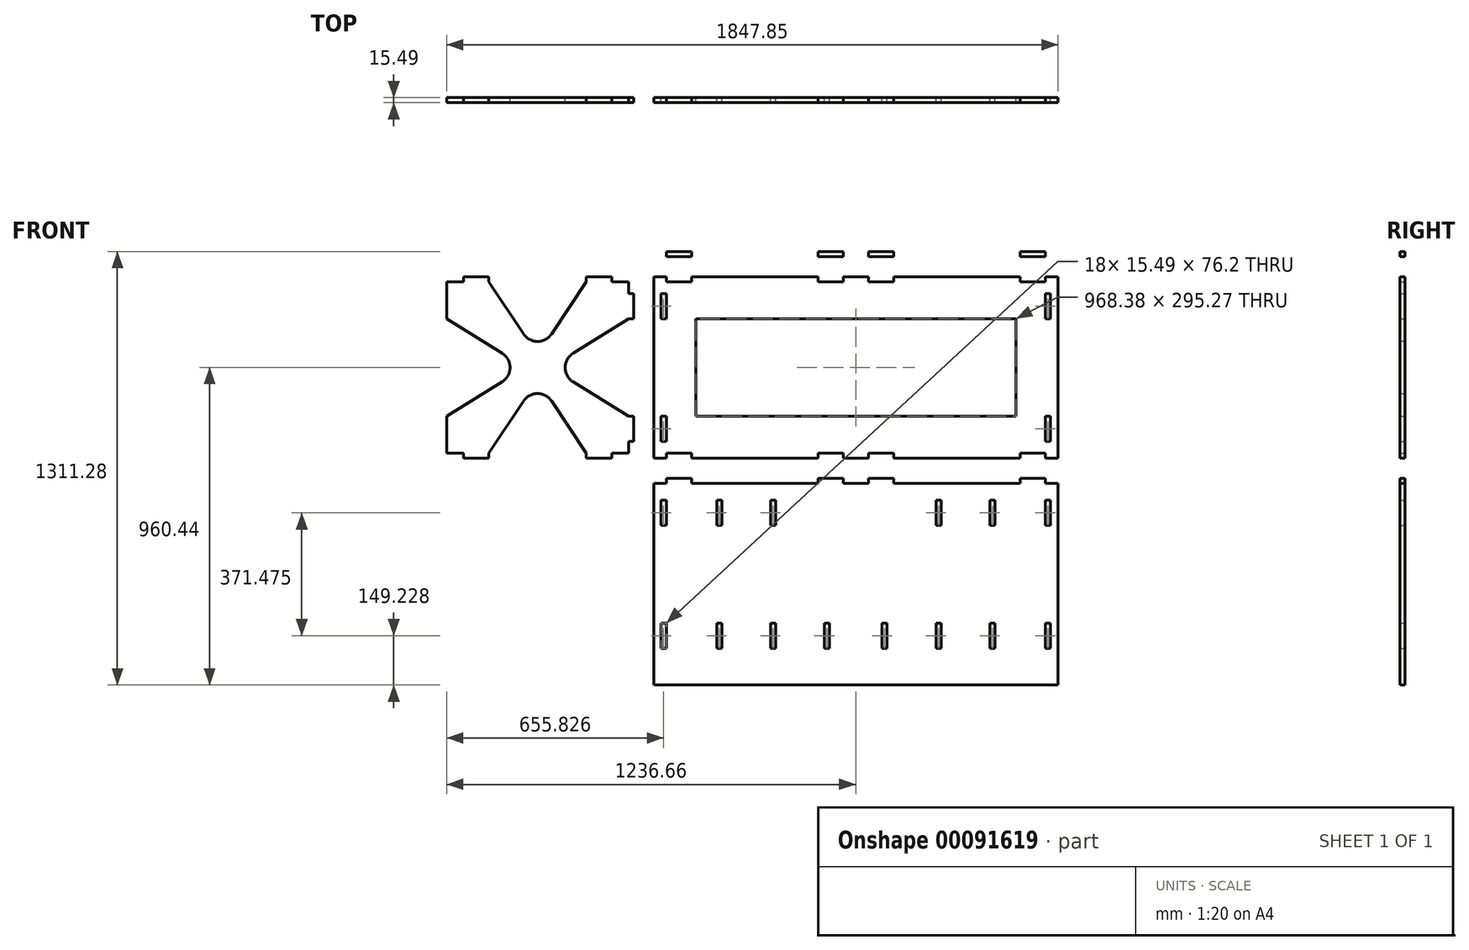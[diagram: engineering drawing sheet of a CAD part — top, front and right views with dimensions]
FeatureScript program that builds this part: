
annotation { "Feature Type Name" : "Feature", "Feature Type Description" : "" }
export const myFeature = defineFeature(function(context is Context, id is Id, definition is map)
    precondition{}
    {
        {
            var Q0;
            Q0=qCreatedBy(makeId("Front.planeOp"),FACE);
            var sketch = newSketch(context, id + "F0", { "sketchPlane" : qUnion([Q0])});
            skLineSegment(sketch, "E0.bottom", {"start": v(611.19, 274.64) * mm, "end": v(-611.19, 274.64) * mm});
            skLineSegment(sketch, "E0.top", {"start": v(611.19, -274.64) * mm, "end": v(-611.19, -274.64) * mm});
            skLineSegment(sketch, "E0.left", {"start": v(611.19, 274.64) * mm, "end": v(611.19, -274.64) * mm});
            skLineSegment(sketch, "E0.right", {"start": v(-611.19, 274.64) * mm, "end": v(-611.19, -274.64) * mm});
            skPoint(sketch, "E0.middle", {"position": v(0, 0) * mm});
            skLineSegment(sketch, "E1.bottom", {"start": v(-573.09, 274.64) * mm, "end": v(-496.89, 274.64) * mm});
            skLineSegment(sketch, "E1.top", {"start": v(-573.09, 258.89) * mm, "end": v(-496.89, 258.89) * mm});
            skLineSegment(sketch, "E1.left", {"start": v(-573.09, 274.64) * mm, "end": v(-573.09, 258.89) * mm});
            skLineSegment(sketch, "E1.right", {"start": v(-496.89, 274.64) * mm, "end": v(-496.89, 258.89) * mm});
            skLineSegment(sketch, "E2", {"start": v(0, 274.64) * mm, "end": v(0, -274.64) * mm, "construction": true});
            skLineSegment(sketch, "E3", {"start": v(-611.19, 0) * mm, "end": v(0, 0) * mm, "construction": true});
            skLineSegment(sketch, "E4", {"start": v(-305.6, -274.64) * mm, "end": v(-305.6, 274.64) * mm, "construction": true});
            skPoint(sketch, "E4.startSnap0", {"position": v(-305.6, 0) * mm});
            skLineSegment(sketch, "E5.MirrorCS", {"start": v(-114.3, 274.64) * mm, "end": v(-114.3, 258.89) * mm});
            skLineSegment(sketch, "E6.MirrorCS", {"start": v(-38.1, 274.64) * mm, "end": v(-38.1, 258.89) * mm});
            skLineSegment(sketch, "E7.MirrorCS", {"start": v(-38.1, 258.89) * mm, "end": v(-114.3, 258.89) * mm});
            skLineSegment(sketch, "E8.MirrorCS", {"start": v(-38.1, 274.64) * mm, "end": v(-114.3, 274.64) * mm});
            skLineSegment(sketch, "E9.MirrorCS", {"start": v(-38.1, -274.64) * mm, "end": v(-38.1, -258.89) * mm});
            skLineSegment(sketch, "E10.MirrorCS", {"start": v(-114.3, -274.64) * mm, "end": v(-114.3, -258.89) * mm});
            skLineSegment(sketch, "E11.MirrorCS", {"start": v(-496.89, -274.64) * mm, "end": v(-496.89, -258.89) * mm});
            skLineSegment(sketch, "E12.MirrorCS", {"start": v(-573.09, -274.64) * mm, "end": v(-573.09, -258.89) * mm});
            skLineSegment(sketch, "E13.MirrorCS", {"start": v(-38.1, -274.64) * mm, "end": v(-114.3, -274.64) * mm});
            skLineSegment(sketch, "E14.MirrorCS", {"start": v(-38.1, -258.89) * mm, "end": v(-114.3, -258.89) * mm});
            skLineSegment(sketch, "E15.MirrorCS", {"start": v(-573.09, -274.64) * mm, "end": v(-496.89, -274.64) * mm});
            skLineSegment(sketch, "E16.MirrorCS", {"start": v(-573.09, -258.89) * mm, "end": v(-496.89, -258.89) * mm});
            skLineSegment(sketch, "E17.MirrorCS", {"start": v(38.1, 274.64) * mm, "end": v(38.1, 258.89) * mm});
            skLineSegment(sketch, "E18.MirrorCS", {"start": v(114.3, 274.64) * mm, "end": v(114.3, 258.89) * mm});
            skLineSegment(sketch, "E19.MirrorCS", {"start": v(496.89, 274.64) * mm, "end": v(496.89, 258.89) * mm});
            skLineSegment(sketch, "E20.MirrorCS", {"start": v(573.09, 274.64) * mm, "end": v(573.09, 258.89) * mm});
            skLineSegment(sketch, "E21.MirrorCS", {"start": v(573.09, 274.64) * mm, "end": v(496.89, 274.64) * mm});
            skLineSegment(sketch, "E22.MirrorCS", {"start": v(573.09, 258.89) * mm, "end": v(496.89, 258.89) * mm});
            skLineSegment(sketch, "E23.MirrorCS", {"start": v(38.1, 274.64) * mm, "end": v(114.3, 274.64) * mm});
            skLineSegment(sketch, "E24.MirrorCS", {"start": v(38.1, 258.89) * mm, "end": v(114.3, 258.89) * mm});
            skLineSegment(sketch, "E25.MirrorCS", {"start": v(573.09, -274.64) * mm, "end": v(573.09, -258.89) * mm});
            skLineSegment(sketch, "E26.MirrorCS", {"start": v(496.89, -274.64) * mm, "end": v(496.89, -258.89) * mm});
            skLineSegment(sketch, "E27.MirrorCS", {"start": v(114.3, -274.64) * mm, "end": v(114.3, -258.89) * mm});
            skLineSegment(sketch, "E28.MirrorCS", {"start": v(38.1, -274.64) * mm, "end": v(38.1, -258.89) * mm});
            skLineSegment(sketch, "E29.MirrorCS", {"start": v(573.09, -258.89) * mm, "end": v(496.89, -258.89) * mm});
            skLineSegment(sketch, "E30.MirrorCS", {"start": v(573.09, -274.64) * mm, "end": v(496.89, -274.64) * mm});
            skLineSegment(sketch, "E31.MirrorCS", {"start": v(38.1, -274.64) * mm, "end": v(114.3, -274.64) * mm});
            skLineSegment(sketch, "E32.MirrorCS", {"start": v(38.1, -258.89) * mm, "end": v(114.3, -258.89) * mm});
            skLineSegment(sketch, "E33.bottom", {"start": v(-573.09, 223.84) * mm, "end": v(-588.58, 223.84) * mm});
            skLineSegment(sketch, "E33.top", {"start": v(-573.09, 147.64) * mm, "end": v(-588.58, 147.64) * mm});
            skLineSegment(sketch, "E33.left", {"start": v(-573.09, 223.84) * mm, "end": v(-573.09, 147.64) * mm});
            skLineSegment(sketch, "E33.right", {"start": v(-588.58, 223.84) * mm, "end": v(-588.58, 147.64) * mm});
            skLineSegment(sketch, "E34.MirrorCS", {"start": v(-573.09, -223.84) * mm, "end": v(-573.09, -147.64) * mm});
            skLineSegment(sketch, "E35.MirrorCS", {"start": v(-588.58, -223.84) * mm, "end": v(-588.58, -147.64) * mm});
            skLineSegment(sketch, "E36.MirrorCS", {"start": v(-573.09, -147.64) * mm, "end": v(-588.58, -147.64) * mm});
            skLineSegment(sketch, "E37.MirrorCS", {"start": v(-573.09, -223.84) * mm, "end": v(-588.58, -223.84) * mm});
            skLineSegment(sketch, "E38.MirrorCS", {"start": v(573.09, -223.84) * mm, "end": v(588.58, -223.84) * mm});
            skLineSegment(sketch, "E39.MirrorCS", {"start": v(573.09, -147.64) * mm, "end": v(588.58, -147.64) * mm});
            skLineSegment(sketch, "E40.MirrorCS", {"start": v(573.09, 223.84) * mm, "end": v(588.58, 223.84) * mm});
            skLineSegment(sketch, "E41.MirrorCS", {"start": v(573.09, 147.64) * mm, "end": v(588.58, 147.64) * mm});
            skLineSegment(sketch, "E42.MirrorCS", {"start": v(573.09, 223.84) * mm, "end": v(573.09, 147.64) * mm});
            skLineSegment(sketch, "E43.MirrorCS", {"start": v(588.58, 223.84) * mm, "end": v(588.58, 147.64) * mm});
            skLineSegment(sketch, "E44.MirrorCS", {"start": v(588.58, -223.84) * mm, "end": v(588.58, -147.64) * mm});
            skLineSegment(sketch, "E45.MirrorCS", {"start": v(573.09, -223.84) * mm, "end": v(573.09, -147.64) * mm});
            skLineSegment(sketch, "E46.bottom", {"start": v(-611.19, 350.84) * mm, "end": v(-3.17, 350.84) * mm});
            skLineSegment(sketch, "E46.top", {"start": v(-611.19, 960.44) * mm, "end": v(-3.18, 960.44) * mm});
            skLineSegment(sketch, "E46.left", {"start": v(-611.19, 350.84) * mm, "end": v(-611.19, 960.44) * mm});
            skLineSegment(sketch, "E46.right", {"start": v(-3.17, 350.84) * mm, "end": v(-3.18, 960.44) * mm});
            skLineSegment(sketch, "E47.bottom", {"start": v(611.19, 350.84) * mm, "end": v(0, 350.84) * mm});
            skLineSegment(sketch, "E47.top", {"start": v(611.19, 960.44) * mm, "end": v(0, 960.44) * mm});
            skLineSegment(sketch, "E47.left", {"start": v(611.19, 350.84) * mm, "end": v(611.19, 960.44) * mm});
            skLineSegment(sketch, "E47.right", {"start": v(0, 350.84) * mm, "end": v(0, 960.44) * mm});
            skLineSegment(sketch, "E48", {"start": v(-76.2, 258.89) * mm, "end": v(-76.2, 350.84) * mm, "construction": true});
            skLineSegment(sketch, "E49", {"start": v(-76.2, 304.86) * mm, "end": v(-114.3, 304.86) * mm, "construction": true});
            skPoint(sketch, "E49.endSnap0", {"position": v(-76.2, 304.86) * mm});
            skLineSegment(sketch, "E50.MirrorCS", {"start": v(496.89, 335.09) * mm, "end": v(496.89, 350.84) * mm});
            skLineSegment(sketch, "E51.MirrorCS", {"start": v(573.09, 335.09) * mm, "end": v(573.09, 350.84) * mm});
            skLineSegment(sketch, "E52.MirrorCS", {"start": v(114.3, 335.09) * mm, "end": v(114.3, 350.84) * mm});
            skLineSegment(sketch, "E53.MirrorCS", {"start": v(-573.09, 335.09) * mm, "end": v(-573.09, 350.84) * mm});
            skLineSegment(sketch, "E54.MirrorCS", {"start": v(-496.89, 335.09) * mm, "end": v(-496.89, 350.84) * mm});
            skLineSegment(sketch, "E55.MirrorCS", {"start": v(38.1, 335.09) * mm, "end": v(38.1, 350.84) * mm});
            skLineSegment(sketch, "E56.MirrorCS", {"start": v(-38.1, 335.09) * mm, "end": v(-38.1, 350.84) * mm});
            skLineSegment(sketch, "E57.MirrorCS", {"start": v(-114.3, 335.09) * mm, "end": v(-114.3, 350.84) * mm});
            skLineSegment(sketch, "E58.MirrorCS", {"start": v(-38.1, 335.09) * mm, "end": v(-114.3, 335.09) * mm});
            skLineSegment(sketch, "E59.MirrorCS", {"start": v(-38.1, 350.84) * mm, "end": v(-114.3, 350.84) * mm});
            skLineSegment(sketch, "E60.MirrorCS", {"start": v(-573.09, 335.09) * mm, "end": v(-496.89, 335.09) * mm});
            skLineSegment(sketch, "E61.MirrorCS", {"start": v(-573.09, 350.84) * mm, "end": v(-496.89, 350.84) * mm});
            skLineSegment(sketch, "E62.MirrorCS", {"start": v(573.09, 335.09) * mm, "end": v(496.89, 335.09) * mm});
            skLineSegment(sketch, "E63.MirrorCS", {"start": v(38.1, 335.09) * mm, "end": v(114.3, 335.09) * mm});
            skLineSegment(sketch, "E64.MirrorCS", {"start": v(573.09, 350.84) * mm, "end": v(496.89, 350.84) * mm});
            skLineSegment(sketch, "E65.MirrorCS", {"start": v(38.1, 350.84) * mm, "end": v(114.3, 350.84) * mm});
            skLineSegment(sketch, "E66", {"start": v(-611.19, 350.84) * mm, "end": v(-611.19, 274.64) * mm, "construction": true});
            skLineSegment(sketch, "E67", {"start": v(-611.19, 312.74) * mm, "end": v(-496.89, 312.74) * mm, "construction": true});
            skLineSegment(sketch, "E68.MirrorCS", {"start": v(-573.09, 773.11) * mm, "end": v(-588.58, 773.11) * mm});
            skLineSegment(sketch, "E69.MirrorCS", {"start": v(-573.09, 477.84) * mm, "end": v(-588.58, 477.84) * mm});
            skLineSegment(sketch, "E70.MirrorCS", {"start": v(-573.09, 401.64) * mm, "end": v(-588.58, 401.64) * mm});
            skLineSegment(sketch, "E71.MirrorCS", {"start": v(-573.09, 849.31) * mm, "end": v(-588.58, 849.31) * mm});
            skLineSegment(sketch, "E72.MirrorCS", {"start": v(-588.58, 401.64) * mm, "end": v(-588.58, 477.84) * mm});
            skLineSegment(sketch, "E73.MirrorCS", {"start": v(-573.09, 849.31) * mm, "end": v(-573.09, 773.11) * mm});
            skLineSegment(sketch, "E74.MirrorCS", {"start": v(-573.09, 401.64) * mm, "end": v(-573.09, 477.84) * mm});
            skLineSegment(sketch, "E75.MirrorCS", {"start": v(-588.58, 849.31) * mm, "end": v(-588.58, 773.11) * mm});
            skLineSegment(sketch, "E76.MirrorCS", {"start": v(573.09, 477.84) * mm, "end": v(588.58, 477.84) * mm});
            skLineSegment(sketch, "E77.MirrorCS", {"start": v(573.09, 401.64) * mm, "end": v(588.58, 401.64) * mm});
            skLineSegment(sketch, "E78.MirrorCS", {"start": v(573.09, 773.11) * mm, "end": v(588.58, 773.11) * mm});
            skLineSegment(sketch, "E79.MirrorCS", {"start": v(573.09, 849.31) * mm, "end": v(588.58, 849.31) * mm});
            skLineSegment(sketch, "E80.MirrorCS", {"start": v(573.09, 401.64) * mm, "end": v(573.09, 477.84) * mm});
            skLineSegment(sketch, "E81.MirrorCS", {"start": v(588.58, 849.31) * mm, "end": v(588.58, 773.11) * mm});
            skLineSegment(sketch, "E82.MirrorCS", {"start": v(573.09, 849.31) * mm, "end": v(573.09, 773.11) * mm});
            skLineSegment(sketch, "E83.MirrorCS", {"start": v(588.58, 401.64) * mm, "end": v(588.58, 477.84) * mm});
            skLineSegment(sketch, "E84.bottom", {"start": v(-687.39, 258.89) * mm, "end": v(-1236.66, 258.89) * mm});
            skLineSegment(sketch, "E84.top", {"start": v(-687.39, -258.89) * mm, "end": v(-1236.66, -258.89) * mm});
            skLineSegment(sketch, "E84.left", {"start": v(-687.39, 258.89) * mm, "end": v(-687.39, -258.89) * mm});
            skLineSegment(sketch, "E84.right", {"start": v(-1236.66, 258.89) * mm, "end": v(-1236.66, -258.89) * mm});
            skLineSegment(sketch, "E85", {"start": v(-738.19, 258.89) * mm, "end": v(-738.19, 274.38) * mm});
            skLineSegment(sketch, "E86", {"start": v(-738.19, 274.38) * mm, "end": v(-814.39, 274.38) * mm});
            skLineSegment(sketch, "E87", {"start": v(-814.39, 274.38) * mm, "end": v(-814.39, 258.89) * mm});
            skLineSegment(sketch, "E88", {"start": v(-687.39, 223.84) * mm, "end": v(-671.9, 223.84) * mm});
            skLineSegment(sketch, "E89", {"start": v(-671.9, 223.84) * mm, "end": v(-671.9, 147.64) * mm});
            skLineSegment(sketch, "E90", {"start": v(-671.9, 147.64) * mm, "end": v(-687.39, 147.64) * mm});
            skLineSegment(sketch, "E91.MirrorCS", {"start": v(-687.39, -223.84) * mm, "end": v(-671.9, -223.84) * mm});
            skLineSegment(sketch, "E92.MirrorCS", {"start": v(-671.9, -147.64) * mm, "end": v(-687.39, -147.64) * mm});
            skLineSegment(sketch, "E93.MirrorCS", {"start": v(-671.9, -223.84) * mm, "end": v(-671.9, -147.64) * mm});
            skLineSegment(sketch, "E94", {"start": v(-962.03, 258.89) * mm, "end": v(-962.03, -258.89) * mm, "construction": true});
            skLineSegment(sketch, "E95", {"start": v(-962.03, -38.1) * mm, "end": v(-1109.66, -258.89) * mm});
            skLineSegment(sketch, "E96", {"start": v(-962.03, -38.1) * mm, "end": v(-814.39, -258.89) * mm});
            skLineSegment(sketch, "E97.bottom", {"start": v(-1000.13, 38.1) * mm, "end": v(-923.93, 38.1) * mm, "construction": true});
            skLineSegment(sketch, "E97.top", {"start": v(-1000.13, -38.1) * mm, "end": v(-923.93, -38.1) * mm, "construction": true});
            skLineSegment(sketch, "E97.left", {"start": v(-1000.13, 38.1) * mm, "end": v(-1000.13, -38.1) * mm, "construction": true});
            skLineSegment(sketch, "E97.right", {"start": v(-923.93, 38.1) * mm, "end": v(-923.93, -38.1) * mm, "construction": true});
            skPoint(sketch, "E97.middle", {"position": v(-962.03, 0) * mm});
            skLineSegment(sketch, "E98", {"start": v(-1000.13, 0) * mm, "end": v(-1236.66, 147.64) * mm});
            skLineSegment(sketch, "E99", {"start": v(-1000.13, 0) * mm, "end": v(-1236.66, -147.64) * mm});
            skLineSegment(sketch, "E100", {"start": v(-962.03, 38.1) * mm, "end": v(-1109.66, 258.89) * mm});
            skLineSegment(sketch, "E101", {"start": v(-814.39, 258.89) * mm, "end": v(-962.03, 38.1) * mm});
            skLineSegment(sketch, "E102", {"start": v(-923.93, 0) * mm, "end": v(-687.39, 147.64) * mm});
            skLineSegment(sketch, "E103", {"start": v(-923.93, 0) * mm, "end": v(-687.39, -147.64) * mm});
            skLineSegment(sketch, "E104.MirrorCS", {"start": v(-573.09, -849.31) * mm, "end": v(-588.58, -849.31) * mm});
            skLineSegment(sketch, "E105.MirrorCS", {"start": v(-573.09, -773.11) * mm, "end": v(-588.58, -773.11) * mm});
            skLineSegment(sketch, "E106.MirrorCS", {"start": v(-573.09, -401.64) * mm, "end": v(-588.58, -401.64) * mm});
            skLineSegment(sketch, "E107.MirrorCS", {"start": v(-114.3, -335.09) * mm, "end": v(-114.3, -350.84) * mm});
            skLineSegment(sketch, "E108.MirrorCS", {"start": v(114.3, -335.09) * mm, "end": v(114.3, -350.84) * mm});
            skLineSegment(sketch, "E109.MirrorCS", {"start": v(-573.09, -477.84) * mm, "end": v(-588.58, -477.84) * mm});
            skLineSegment(sketch, "E110.MirrorCS", {"start": v(-573.09, -335.09) * mm, "end": v(-573.09, -350.84) * mm});
            skLineSegment(sketch, "E111.MirrorCS", {"start": v(-496.89, -335.09) * mm, "end": v(-496.89, -350.84) * mm});
            skLineSegment(sketch, "E112.MirrorCS", {"start": v(38.1, -335.09) * mm, "end": v(38.1, -350.84) * mm});
            skLineSegment(sketch, "E113.MirrorCS", {"start": v(-38.1, -335.09) * mm, "end": v(-38.1, -350.84) * mm});
            skLineSegment(sketch, "E114.MirrorCS", {"start": v(573.09, -477.84) * mm, "end": v(588.58, -477.84) * mm});
            skLineSegment(sketch, "E115.MirrorCS", {"start": v(573.09, -773.11) * mm, "end": v(588.58, -773.11) * mm});
            skLineSegment(sketch, "E116.MirrorCS", {"start": v(573.09, -401.64) * mm, "end": v(588.58, -401.64) * mm});
            skLineSegment(sketch, "E117.MirrorCS", {"start": v(573.09, -849.31) * mm, "end": v(588.58, -849.31) * mm});
            skLineSegment(sketch, "E118.MirrorCS", {"start": v(496.89, -335.09) * mm, "end": v(496.89, -350.84) * mm});
            skLineSegment(sketch, "E119.MirrorCS", {"start": v(573.09, -335.09) * mm, "end": v(573.09, -350.84) * mm});
            skLineSegment(sketch, "E120.MirrorCS", {"start": v(-38.1, -335.09) * mm, "end": v(-114.3, -335.09) * mm});
            skLineSegment(sketch, "E121.MirrorCS", {"start": v(-38.1, -350.84) * mm, "end": v(-114.3, -350.84) * mm});
            skLineSegment(sketch, "E122.MirrorCS", {"start": v(-588.58, -401.64) * mm, "end": v(-588.58, -477.84) * mm});
            skLineSegment(sketch, "E123.MirrorCS", {"start": v(-573.09, -849.31) * mm, "end": v(-573.09, -773.11) * mm});
            skLineSegment(sketch, "E124.MirrorCS", {"start": v(-573.09, -401.64) * mm, "end": v(-573.09, -477.84) * mm});
            skLineSegment(sketch, "E125.MirrorCS", {"start": v(-588.58, -849.31) * mm, "end": v(-588.58, -773.11) * mm});
            skLineSegment(sketch, "E126.MirrorCS", {"start": v(-573.09, -335.09) * mm, "end": v(-496.89, -335.09) * mm});
            skLineSegment(sketch, "E127.MirrorCS", {"start": v(573.09, -335.09) * mm, "end": v(496.89, -335.09) * mm});
            skLineSegment(sketch, "E128.MirrorCS", {"start": v(-573.09, -350.84) * mm, "end": v(-496.89, -350.84) * mm});
            skLineSegment(sketch, "E129.MirrorCS", {"start": v(38.1, -335.09) * mm, "end": v(114.3, -335.09) * mm});
            skLineSegment(sketch, "E130.MirrorCS", {"start": v(573.09, -350.84) * mm, "end": v(496.89, -350.84) * mm});
            skLineSegment(sketch, "E131.MirrorCS", {"start": v(573.09, -401.64) * mm, "end": v(573.09, -477.84) * mm});
            skLineSegment(sketch, "E132.MirrorCS", {"start": v(588.58, -849.31) * mm, "end": v(588.58, -773.11) * mm});
            skLineSegment(sketch, "E133.MirrorCS", {"start": v(38.1, -350.84) * mm, "end": v(114.3, -350.84) * mm});
            skLineSegment(sketch, "E134.MirrorCS", {"start": v(573.09, -849.31) * mm, "end": v(573.09, -773.11) * mm});
            skLineSegment(sketch, "E135.MirrorCS", {"start": v(588.58, -401.64) * mm, "end": v(588.58, -477.84) * mm});
            skLineSegment(sketch, "E136.MirrorCS", {"start": v(-611.19, -350.84) * mm, "end": v(-611.19, -960.44) * mm});
            skLineSegment(sketch, "E137.MirrorCS", {"start": v(611.19, -350.84) * mm, "end": v(611.19, -960.44) * mm});
            skLineSegment(sketch, "E138", {"start": v(-611.19, -350.84) * mm, "end": v(611.19, -350.84) * mm});
            skLineSegment(sketch, "E139", {"start": v(611.19, -960.44) * mm, "end": v(-611.19, -960.44) * mm});
            skLineSegment(sketch, "E140.MirrorCS", {"start": v(-738.19, -258.89) * mm, "end": v(-738.19, -274.38) * mm});
            skLineSegment(sketch, "E141.MirrorCS", {"start": v(-814.39, -274.38) * mm, "end": v(-814.39, -258.89) * mm});
            skLineSegment(sketch, "E142.MirrorCS", {"start": v(-738.19, -274.38) * mm, "end": v(-814.39, -274.38) * mm});
            skLineSegment(sketch, "E143", {"start": v(-496.89, 223.84) * mm, "end": v(-496.89, -223.84) * mm, "construction": true});
            skLineSegment(sketch, "E144", {"start": v(-738.19, -350.84) * mm, "end": v(-1185.86, -350.84) * mm});
            skPoint(sketch, "E145", {"position": v(-962.03, -350.84) * mm});
            skLineSegment(sketch, "E146.MirrorCS", {"start": v(-1109.66, -274.38) * mm, "end": v(-1109.66, -258.89) * mm});
            skLineSegment(sketch, "E147.MirrorCS", {"start": v(-1185.86, -274.38) * mm, "end": v(-1109.66, -274.38) * mm});
            skLineSegment(sketch, "E148.MirrorCS", {"start": v(-1185.86, -258.89) * mm, "end": v(-1185.86, -274.38) * mm});
            skLineSegment(sketch, "E149.MirrorCS", {"start": v(-1185.86, 258.89) * mm, "end": v(-1185.86, 274.38) * mm});
            skLineSegment(sketch, "E150.MirrorCS", {"start": v(-1185.86, 274.38) * mm, "end": v(-1109.66, 274.38) * mm});
            skLineSegment(sketch, "E151.MirrorCS", {"start": v(-1109.66, 274.38) * mm, "end": v(-1109.66, 258.89) * mm});
            skLineSegment(sketch, "E152", {"start": v(-333.98, 960.44) * mm, "end": v(-333.98, 350.84) * mm, "construction": true});
            skLineSegment(sketch, "E153.MirrorCS", {"start": v(-94.87, 477.84) * mm, "end": v(-79.37, 477.84) * mm});
            skLineSegment(sketch, "E154.MirrorCS", {"start": v(-94.87, 773.11) * mm, "end": v(-79.38, 773.11) * mm});
            skLineSegment(sketch, "E155.MirrorCS", {"start": v(-94.87, 401.64) * mm, "end": v(-79.38, 401.64) * mm});
            skLineSegment(sketch, "E156.MirrorCS", {"start": v(-94.87, 849.31) * mm, "end": v(-79.38, 849.31) * mm});
            skLineSegment(sketch, "E157.MirrorCS", {"start": v(-79.37, 401.64) * mm, "end": v(-79.37, 477.84) * mm});
            skLineSegment(sketch, "E158.MirrorCS", {"start": v(-94.87, 849.31) * mm, "end": v(-94.87, 773.11) * mm});
            skLineSegment(sketch, "E159.MirrorCS", {"start": v(-79.38, 849.31) * mm, "end": v(-79.38, 773.11) * mm});
            skLineSegment(sketch, "E160.MirrorCS", {"start": v(-94.87, 401.64) * mm, "end": v(-94.87, 477.84) * mm});
            skLineSegment(sketch, "E161.MirrorCS", {"start": v(94.87, 477.84) * mm, "end": v(79.37, 477.84) * mm});
            skLineSegment(sketch, "E162.MirrorCS", {"start": v(94.87, 773.11) * mm, "end": v(79.37, 773.11) * mm});
            skLineSegment(sketch, "E163.MirrorCS", {"start": v(94.87, 401.64) * mm, "end": v(79.37, 401.64) * mm});
            skLineSegment(sketch, "E164.MirrorCS", {"start": v(94.87, 849.31) * mm, "end": v(79.37, 849.31) * mm});
            skLineSegment(sketch, "E165.MirrorCS", {"start": v(79.37, 849.31) * mm, "end": v(79.37, 773.11) * mm});
            skLineSegment(sketch, "E166.MirrorCS", {"start": v(94.87, 401.64) * mm, "end": v(94.87, 477.84) * mm});
            skLineSegment(sketch, "E167.MirrorCS", {"start": v(94.87, 849.31) * mm, "end": v(94.87, 773.11) * mm});
            skLineSegment(sketch, "E168.MirrorCS", {"start": v(79.37, 401.64) * mm, "end": v(79.37, 477.84) * mm});
            skLineSegment(sketch, "E169.bottom", {"start": v(-420.69, 849.31) * mm, "end": v(-405.2, 849.31) * mm});
            skLineSegment(sketch, "E169.top", {"start": v(-420.69, 773.11) * mm, "end": v(-405.2, 773.11) * mm});
            skLineSegment(sketch, "E169.left", {"start": v(-420.69, 849.31) * mm, "end": v(-420.69, 773.11) * mm});
            skLineSegment(sketch, "E169.right", {"start": v(-405.2, 849.31) * mm, "end": v(-405.2, 773.11) * mm});
            skLineSegment(sketch, "E170", {"start": v(-405.2, 811.21) * mm, "end": v(-94.87, 811.21) * mm, "construction": true});
            skLineSegment(sketch, "E171.bottom", {"start": v(-257.78, 849.31) * mm, "end": v(-242.28, 849.31) * mm});
            skLineSegment(sketch, "E171.top", {"start": v(-257.78, 773.11) * mm, "end": v(-242.28, 773.11) * mm});
            skLineSegment(sketch, "E171.left", {"start": v(-257.78, 849.31) * mm, "end": v(-257.78, 773.11) * mm});
            skLineSegment(sketch, "E171.right", {"start": v(-242.28, 849.31) * mm, "end": v(-242.28, 773.11) * mm});
            skPoint(sketch, "E171.middle", {"position": v(-250.03, 811.21) * mm});
            skLineSegment(sketch, "E172.MirrorCS", {"start": v(257.78, 773.11) * mm, "end": v(242.28, 773.11) * mm});
            skLineSegment(sketch, "E173.MirrorCS", {"start": v(420.69, 773.11) * mm, "end": v(405.2, 773.11) * mm});
            skLineSegment(sketch, "E174.MirrorCS", {"start": v(257.78, 849.31) * mm, "end": v(242.28, 849.31) * mm});
            skLineSegment(sketch, "E175.MirrorCS", {"start": v(420.69, 849.31) * mm, "end": v(405.2, 849.31) * mm});
            skLineSegment(sketch, "E176.MirrorCS", {"start": v(420.69, 849.31) * mm, "end": v(420.69, 773.11) * mm});
            skLineSegment(sketch, "E177.MirrorCS", {"start": v(405.2, 849.31) * mm, "end": v(405.2, 773.11) * mm});
            skLineSegment(sketch, "E178.MirrorCS", {"start": v(257.78, 849.31) * mm, "end": v(257.78, 773.11) * mm});
            skLineSegment(sketch, "E179.MirrorCS", {"start": v(242.28, 849.31) * mm, "end": v(242.28, 773.11) * mm});
            skPoint(sketch, "E180.MirrorP", {"position": v(250.03, 811.21) * mm});
            skLineSegment(sketch, "E181.MirrorCS", {"start": v(-420.69, -773.11) * mm, "end": v(-405.2, -773.11) * mm});
            skLineSegment(sketch, "E182.MirrorCS", {"start": v(-257.78, -773.11) * mm, "end": v(-242.28, -773.11) * mm});
            skLineSegment(sketch, "E183.MirrorCS", {"start": v(-79.37, -849.31) * mm, "end": v(-79.37, -773.11) * mm});
            skLineSegment(sketch, "E184.MirrorCS", {"start": v(94.87, -773.11) * mm, "end": v(79.38, -773.11) * mm});
            skLineSegment(sketch, "E185.MirrorCS", {"start": v(420.69, -773.11) * mm, "end": v(405.2, -773.11) * mm});
            skLineSegment(sketch, "E186.MirrorCS", {"start": v(79.38, -849.31) * mm, "end": v(79.37, -773.11) * mm});
            skLineSegment(sketch, "E187.MirrorCS", {"start": v(420.69, -849.31) * mm, "end": v(420.69, -773.11) * mm});
            skLineSegment(sketch, "E188.MirrorCS", {"start": v(94.87, -849.31) * mm, "end": v(79.38, -849.31) * mm});
            skLineSegment(sketch, "E189.MirrorCS", {"start": v(-242.28, -849.31) * mm, "end": v(-242.28, -773.11) * mm});
            skLineSegment(sketch, "E190.MirrorCS", {"start": v(-257.78, -849.31) * mm, "end": v(-242.28, -849.31) * mm});
            skLineSegment(sketch, "E191.MirrorCS", {"start": v(257.78, -849.31) * mm, "end": v(242.28, -849.31) * mm});
            skLineSegment(sketch, "E192.MirrorCS", {"start": v(-94.87, -849.31) * mm, "end": v(-79.37, -849.31) * mm});
            skLineSegment(sketch, "E193.MirrorCS", {"start": v(257.78, -849.31) * mm, "end": v(257.78, -773.11) * mm});
            skLineSegment(sketch, "E194.MirrorCS", {"start": v(242.28, -849.31) * mm, "end": v(242.28, -773.11) * mm});
            skLineSegment(sketch, "E195.MirrorCS", {"start": v(-420.69, -849.31) * mm, "end": v(-405.2, -849.31) * mm});
            skLineSegment(sketch, "E196.MirrorCS", {"start": v(-94.87, -773.11) * mm, "end": v(-79.37, -773.11) * mm});
            skLineSegment(sketch, "E197.MirrorCS", {"start": v(257.78, -773.11) * mm, "end": v(242.28, -773.11) * mm});
            skLineSegment(sketch, "E198.MirrorCS", {"start": v(-405.2, -849.31) * mm, "end": v(-405.2, -773.11) * mm});
            skLineSegment(sketch, "E199.MirrorCS", {"start": v(-420.69, -849.31) * mm, "end": v(-420.69, -773.11) * mm});
            skLineSegment(sketch, "E200.MirrorCS", {"start": v(-94.87, -849.31) * mm, "end": v(-94.87, -773.11) * mm});
            skLineSegment(sketch, "E201.MirrorCS", {"start": v(-257.78, -849.31) * mm, "end": v(-257.78, -773.11) * mm});
            skLineSegment(sketch, "E202.MirrorCS", {"start": v(420.69, -849.31) * mm, "end": v(405.2, -849.31) * mm});
            skLineSegment(sketch, "E203.MirrorCS", {"start": v(405.2, -849.31) * mm, "end": v(405.2, -773.11) * mm});
            skLineSegment(sketch, "E204.MirrorCS", {"start": v(94.87, -849.31) * mm, "end": v(94.87, -773.11) * mm});
            skPoint(sketch, "E205.MirrorP", {"position": v(250.03, -811.21) * mm});
            skPoint(sketch, "E206.MirrorP", {"position": v(-250.03, -811.21) * mm});
            skLineSegment(sketch, "E207.MirrorCS", {"start": v(-405.2, -811.21) * mm, "end": v(-94.87, -811.21) * mm, "construction": true});
            skLineSegment(sketch, "E208", {"start": v(-333.98, 849.31) * mm, "end": v(-333.98, 401.64) * mm, "construction": true});
            skLineSegment(sketch, "E209", {"start": v(-333.98, 625.48) * mm, "end": v(-420.69, 625.48) * mm, "construction": true});
            skLineSegment(sketch, "E210.MirrorCS", {"start": v(-257.78, 401.64) * mm, "end": v(-242.28, 401.64) * mm});
            skLineSegment(sketch, "E211.MirrorCS", {"start": v(-257.78, 477.84) * mm, "end": v(-242.28, 477.84) * mm});
            skLineSegment(sketch, "E212.MirrorCS", {"start": v(-420.69, 477.84) * mm, "end": v(-405.2, 477.84) * mm});
            skLineSegment(sketch, "E213.MirrorCS", {"start": v(-420.69, 401.64) * mm, "end": v(-405.2, 401.64) * mm});
            skLineSegment(sketch, "E214.MirrorCS", {"start": v(-242.28, 401.64) * mm, "end": v(-242.28, 477.84) * mm});
            skLineSegment(sketch, "E215.MirrorCS", {"start": v(-257.78, 401.64) * mm, "end": v(-257.78, 477.84) * mm});
            skLineSegment(sketch, "E216.MirrorCS", {"start": v(-405.2, 401.64) * mm, "end": v(-405.2, 477.84) * mm});
            skPoint(sketch, "E217.MirrorP", {"position": v(-250.03, 439.74) * mm});
            skLineSegment(sketch, "E218.MirrorCS", {"start": v(-420.69, 401.64) * mm, "end": v(-420.69, 477.84) * mm});
            skLineSegment(sketch, "E219.MirrorCS", {"start": v(420.69, 401.64) * mm, "end": v(405.2, 401.64) * mm});
            skLineSegment(sketch, "E220.MirrorCS", {"start": v(257.78, 401.64) * mm, "end": v(242.28, 401.64) * mm});
            skLineSegment(sketch, "E221.MirrorCS", {"start": v(257.78, 477.84) * mm, "end": v(242.28, 477.84) * mm});
            skLineSegment(sketch, "E222.MirrorCS", {"start": v(420.69, 477.84) * mm, "end": v(405.2, 477.84) * mm});
            skLineSegment(sketch, "E223.MirrorCS", {"start": v(257.78, 401.64) * mm, "end": v(257.78, 477.84) * mm});
            skLineSegment(sketch, "E224.MirrorCS", {"start": v(242.28, 401.64) * mm, "end": v(242.28, 477.84) * mm});
            skPoint(sketch, "E225.MirrorP", {"position": v(250.03, 439.74) * mm});
            skLineSegment(sketch, "E226.MirrorCS", {"start": v(420.69, 401.64) * mm, "end": v(420.69, 477.84) * mm});
            skLineSegment(sketch, "E227.MirrorCS", {"start": v(405.2, 401.64) * mm, "end": v(405.2, 477.84) * mm});
            skLineSegment(sketch, "E228.MirrorCS", {"start": v(-257.78, -477.84) * mm, "end": v(-242.28, -477.84) * mm});
            skLineSegment(sketch, "E229.MirrorCS", {"start": v(-420.69, -477.84) * mm, "end": v(-405.2, -477.84) * mm});
            skLineSegment(sketch, "E230.MirrorCS", {"start": v(-257.78, -401.64) * mm, "end": v(-242.28, -401.64) * mm});
            skLineSegment(sketch, "E231.MirrorCS", {"start": v(-420.69, -401.64) * mm, "end": v(-405.2, -401.64) * mm});
            skLineSegment(sketch, "E232.MirrorCS", {"start": v(-242.28, -401.64) * mm, "end": v(-242.28, -477.84) * mm});
            skPoint(sketch, "E233.MirrorP", {"position": v(-250.03, -439.74) * mm});
            skLineSegment(sketch, "E234.MirrorCS", {"start": v(-420.69, -401.64) * mm, "end": v(-420.69, -477.84) * mm});
            skLineSegment(sketch, "E235.MirrorCS", {"start": v(-257.78, -401.64) * mm, "end": v(-257.78, -477.84) * mm});
            skLineSegment(sketch, "E236.MirrorCS", {"start": v(-405.2, -401.64) * mm, "end": v(-405.2, -477.84) * mm});
            skLineSegment(sketch, "E237.MirrorCS", {"start": v(420.69, -401.64) * mm, "end": v(405.2, -401.64) * mm});
            skLineSegment(sketch, "E238.MirrorCS", {"start": v(257.78, -401.64) * mm, "end": v(242.28, -401.64) * mm});
            skLineSegment(sketch, "E239.MirrorCS", {"start": v(257.78, -477.84) * mm, "end": v(242.28, -477.84) * mm});
            skLineSegment(sketch, "E240.MirrorCS", {"start": v(420.69, -477.84) * mm, "end": v(405.2, -477.84) * mm});
            skLineSegment(sketch, "E241.MirrorCS", {"start": v(257.78, -401.64) * mm, "end": v(257.78, -477.84) * mm});
            skLineSegment(sketch, "E242.MirrorCS", {"start": v(242.28, -401.64) * mm, "end": v(242.28, -477.84) * mm});
            skPoint(sketch, "E243.MirrorP", {"position": v(250.03, -439.74) * mm});
            skLineSegment(sketch, "E244.MirrorCS", {"start": v(405.2, -401.64) * mm, "end": v(405.2, -477.84) * mm});
            skLineSegment(sketch, "E245.MirrorCS", {"start": v(420.69, -401.64) * mm, "end": v(420.69, -477.84) * mm});
            skLineSegment(sketch, "E246.bottom", {"start": v(-484.19, 147.64) * mm, "end": v(484.19, 147.64) * mm});
            skLineSegment(sketch, "E246.top", {"start": v(-484.19, -147.64) * mm, "end": v(484.19, -147.64) * mm});
            skLineSegment(sketch, "E246.left", {"start": v(-484.19, 147.64) * mm, "end": v(-484.19, -147.64) * mm});
            skLineSegment(sketch, "E246.right", {"start": v(484.19, 147.64) * mm, "end": v(484.19, -147.64) * mm});
            skSolve(sketch);
        }
        {
            var Q0;
            Q0=makeQuery(id+"F0.imprint","IMPRINT",FACE,{"disambiguationData":[TD([[makeQuery(id+"F0.imprint","IMPRINT",EDGE,{"derivedFrom":sQuery(id+"F0.wireOp",EDGE,"92eabbe3-f8f1-4d0b-bcb1-c722cdc1d4602.MirrorCS")}),-1.0]])]});
            var Q1;
            {var subQ0=sQuery(id+"F0.wireOp",EDGE,"92eabbe3-f8f1-4d0b-bcb1-c722cdc1d4600.MirrorCS");Q1=makeQuery(id+"F0.imprint","IMPRINT",FACE,{"disambiguationData":[TD([[makeQuery(id+"F0.imprint","IMPRINT",EDGE,{"derivedFrom":subQ0}),1.0]])]});}
            var Q2;
            {var subQ0=sQuery(id+"F0.wireOp",EDGE,"E85");Q2=makeQuery(id+"F0.imprint","IMPRINT",FACE,{"disambiguationData":[TD([[makeQuery(id+"F0.imprint","IMPRINT",EDGE,{"derivedFrom":subQ0}),1.0]])]});}
            var Q3;
            {var subQ0=sQuery(id+"F0.wireOp",EDGE,"E88");Q3=makeQuery(id+"F0.imprint","IMPRINT",FACE,{"disambiguationData":[TD([[makeQuery(id+"F0.imprint","IMPRINT",EDGE,{"derivedFrom":subQ0}),-1.0]])]});}
            var Q4;
            {var subQ0=sQuery(id+"F0.wireOp",EDGE,"E91.MirrorCS");Q4=makeQuery(id+"F0.imprint","IMPRINT",FACE,{"disambiguationData":[TD([[makeQuery(id+"F0.imprint","IMPRINT",EDGE,{"derivedFrom":subQ0}),1.0]])]});}
            var Q5;
            Q5=makeQuery(id+"F0.imprint","IMPRINT",FACE,{"disambiguationData":[TD([[makeQuery(id+"F0.imprint","IMPRINT",EDGE,{"derivedFrom":sQuery(id+"F0.wireOp",EDGE,"58aca8fd-671b-425e-b90f-f2314bb2d9823.MirrorCS")}),-1.0]])]});
            var Q6;
            {var subQ0=sQuery(id+"F0.wireOp",EDGE,"5484c05e-e100-47fc-b072-6ca6ee2ab5f80.MirrorCS");Q6=makeQuery(id+"F0.imprint","IMPRINT",FACE,{"disambiguationData":[TD([[makeQuery(id+"F0.imprint","IMPRINT",EDGE,{"derivedFrom":subQ0}),1.0]])]});}
            var Q7;
            {var subQ0=sQuery(id+"F0.wireOp",EDGE,"5484c05e-e100-47fc-b072-6ca6ee2ab5f82.MirrorCS");Q7=makeQuery(id+"F0.imprint","IMPRINT",FACE,{"disambiguationData":[TD([[makeQuery(id+"F0.imprint","IMPRINT",EDGE,{"derivedFrom":subQ0}),-1.0]])]});}
            var Q8;
            Q8=makeQuery(id+"F0.imprint","IMPRINT",FACE,{"disambiguationData":[TD([[makeQuery(id+"F0.imprint","IMPRINT",EDGE,{"derivedFrom":sQuery(id+"F0.wireOp",EDGE,"E53.MirrorCS")}),-1.0]])]});
            var Q9;
            Q9=makeQuery(id+"F0.imprint","IMPRINT",FACE,{"disambiguationData":[TD([[makeQuery(id+"F0.imprint","IMPRINT",EDGE,{"derivedFrom":sQuery(id+"F0.wireOp",EDGE,"E56.MirrorCS")}),1.0]])]});
            var Q10;
            Q10=makeQuery(id+"F0.imprint","IMPRINT",FACE,{"disambiguationData":[TD([[makeQuery(id+"F0.imprint","IMPRINT",EDGE,{"derivedFrom":sQuery(id+"F0.wireOp",EDGE,"E52.MirrorCS")}),1.0]])]});
            var Q11;
            Q11=makeQuery(id+"F0.imprint","IMPRINT",FACE,{"disambiguationData":[TD([[makeQuery(id+"F0.imprint","IMPRINT",EDGE,{"derivedFrom":sQuery(id+"F0.wireOp",EDGE,"E50.MirrorCS")}),-1.0]])]});
            var Q12;
            Q12=makeQuery(id+"F0.imprint","IMPRINT",FACE,{"disambiguationData":[TD([[makeQuery(id+"F0.imprint","IMPRINT",EDGE,{"derivedFrom":sQuery(id+"F0.wireOp",EDGE,"E104.MirrorCS")}),1.0]])]});
            var Q13;
            {var subQ0=sQuery(id+"F0.wireOp",EDGE,"E110.MirrorCS");Q13=makeQuery(id+"F0.imprint","IMPRINT",FACE,{"disambiguationData":[TD([[makeQuery(id+"F0.imprint","IMPRINT",EDGE,{"derivedFrom":subQ0}),1.0]])]});}
            var Q14;
            {var subQ0=sQuery(id+"F0.wireOp",EDGE,"E118.MirrorCS");Q14=makeQuery(id+"F0.imprint","IMPRINT",FACE,{"disambiguationData":[TD([[makeQuery(id+"F0.imprint","IMPRINT",EDGE,{"derivedFrom":subQ0}),1.0]])]});}
            var Q15;
            {var subQ0=sQuery(id+"F0.wireOp",EDGE,"E107.MirrorCS");Q15=makeQuery(id+"F0.imprint","IMPRINT",FACE,{"disambiguationData":[TD([[makeQuery(id+"F0.imprint","IMPRINT",EDGE,{"derivedFrom":subQ0}),1.0]])]});}
            var Q16;
            {var subQ0=sQuery(id+"F0.wireOp",EDGE,"E108.MirrorCS");Q16=makeQuery(id+"F0.imprint","IMPRINT",FACE,{"disambiguationData":[TD([[makeQuery(id+"F0.imprint","IMPRINT",EDGE,{"derivedFrom":subQ0}),-1.0]])]});}
            var Q17;
            {var subQ2=sQuery(id+"F0.wireOp",EDGE,"E95");Q17=makeQuery(id+"F0.imprint","IMPRINT",FACE,{"disambiguationData":[TD([[makeQuery(id+"F0.imprint","IMPRINT",EDGE,{"derivedFrom":subQ2}),-1.0]])]});}
            var Q18;
            {var subQ1=sQuery(id+"F0.wireOp",EDGE,"E0.left");Q18=makeQuery(id+"F0.imprint","IMPRINT",FACE,{"disambiguationData":[TD([[makeQuery(id+"F0.imprint","IMPRINT",EDGE,{"derivedFrom":subQ1}),-1.0]])]});}
            var Q19;
            {var subQ2=sQuery(id+"F0.wireOp",EDGE,"E149.MirrorCS");Q19=makeQuery(id+"F0.imprint","IMPRINT",FACE,{"disambiguationData":[TD([[makeQuery(id+"F0.imprint","IMPRINT",EDGE,{"derivedFrom":subQ2}),-1.0]])]});}
            var Q20;
            {var subQ0=sQuery(id+"F0.wireOp",EDGE,"E146.MirrorCS");Q20=makeQuery(id+"F0.imprint","IMPRINT",FACE,{"disambiguationData":[TD([[makeQuery(id+"F0.imprint","IMPRINT",EDGE,{"derivedFrom":subQ0}),1.0]])]});}
            var Q21;
            {var subQ3=sQuery(id+"F0.wireOp",EDGE,"E59.MirrorCS");Q21=makeQuery(id+"F0.imprint","IMPRINT",FACE,{"disambiguationData":[TD([[makeQuery(id+"F0.imprint","IMPRINT",EDGE,{"derivedFrom":subQ3}),-1.0]])]});}
            var Q22;
            {var subQ7=sQuery(id+"F0.wireOp",EDGE,"E64.MirrorCS");Q22=makeQuery(id+"F0.imprint","IMPRINT",FACE,{"disambiguationData":[TD([[makeQuery(id+"F0.imprint","IMPRINT",EDGE,{"derivedFrom":subQ7}),-1.0]])]});}
            var Q23;
            {var subQ2=sQuery(id+"F0.wireOp",EDGE,"E140.MirrorCS");Q23=makeQuery(id+"F0.imprint","IMPRINT",FACE,{"disambiguationData":[TD([[makeQuery(id+"F0.imprint","IMPRINT",EDGE,{"derivedFrom":subQ2}),-1.0]])]});}
            extrude(context, id + "F1", {"entities" : qUnion([Q0, Q1, Q2, Q3, Q4, Q5, Q6, Q7, Q8, Q9, Q10, Q11, Q12, Q13, Q14, Q15, Q16, Q17, Q18, Q19, Q20, Q21, Q22, Q23]), "depth" : 15.5 * mm});
        }
        {
            var Q0;
            Q0=makeQuery(id+"F1.opExtrude","SWEPT_EDGE",EDGE,{"disambiguationData":[OSD([sQuery(id+"F0.wireOp",EDGE,"E98"),sQuery(id+"F0.wireOp",EDGE,"E99")])]});
            var Q1;
            Q1=makeQuery(id+"F1.opExtrude","SWEPT_EDGE",EDGE,{"disambiguationData":[OSD([sQuery(id+"F0.wireOp",EDGE,"E100"),sQuery(id+"F0.wireOp",EDGE,"E101")])]});
            var Q2;
            Q2=makeQuery(id+"F1.opExtrude","SWEPT_EDGE",EDGE,{"disambiguationData":[OSD([sQuery(id+"F0.wireOp",EDGE,"E102"),sQuery(id+"F0.wireOp",EDGE,"E103")])]});
            var Q3;
            Q3=makeQuery(id+"F1.opExtrude","SWEPT_EDGE",EDGE,{"disambiguationData":[OSD([sQuery(id+"F0.wireOp",EDGE,"E95"),sQuery(id+"F0.wireOp",EDGE,"E96")])]});
            fillet(context, id + "F2", {"entities" : qUnion([Q0, Q1, Q2, Q3]), "radius" : 50.8 * mm, "tangentPropagation" : true, "allowEdgeOverflow" : false});
        }
    });
